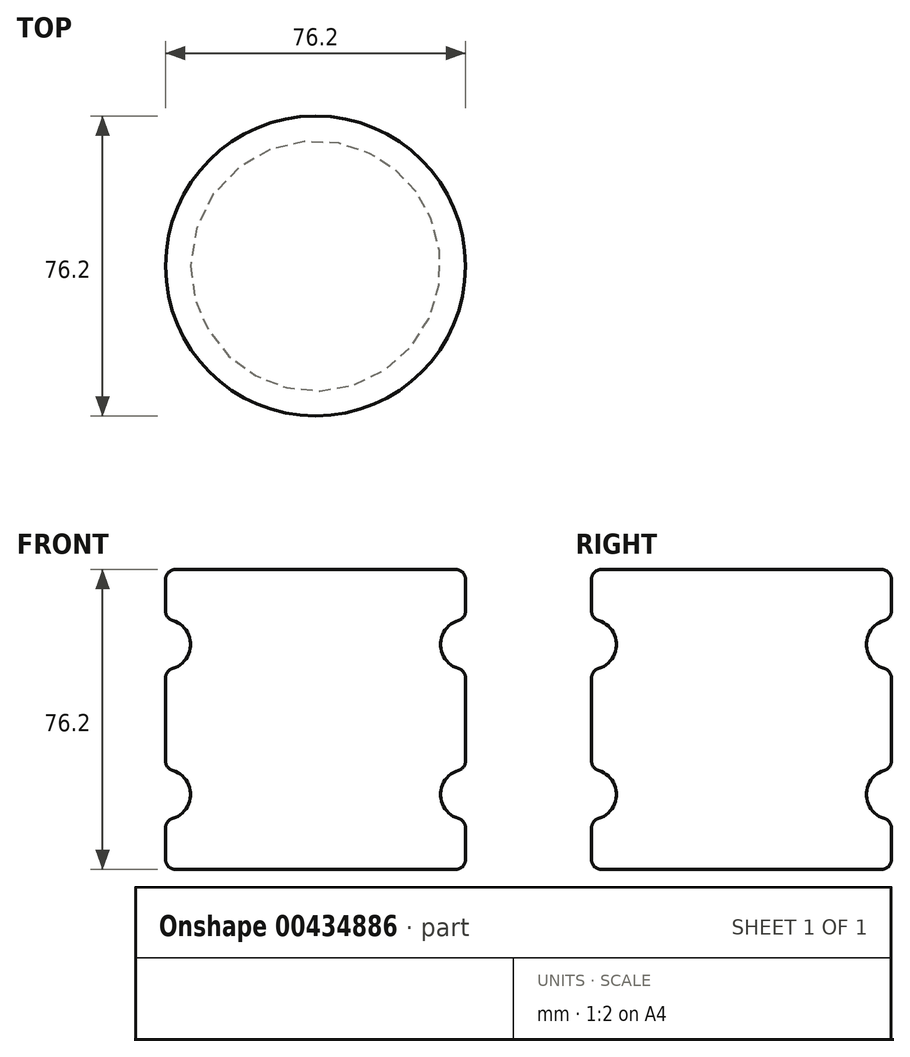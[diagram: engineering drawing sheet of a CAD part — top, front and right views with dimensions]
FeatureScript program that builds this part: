
annotation { "Feature Type Name" : "Feature", "Feature Type Description" : "" }
export const myFeature = defineFeature(function(context is Context, id is Id, definition is map)
    precondition{}
    {
        {
            var Q0;
            Q0=qCreatedBy(makeId("Front.planeOp"),FACE);
            var sketch = newSketch(context, id + "F0", { "sketchPlane" : qUnion([Q0])});
            skLineSegment(sketch, "E0.bottom", {"start": v(0, 0) * mm, "end": v(-38.1, 0) * mm});
            skLineSegment(sketch, "E0.top", {"start": v(0, 76.2) * mm, "end": v(-38.1, 76.2) * mm});
            skLineSegment(sketch, "E0.left", {"start": v(0, 0) * mm, "end": v(0, 76.2) * mm});
            skLineSegment(sketch, "E0.right", {"start": v(-38.1, 0) * mm, "end": v(-38.1, 76.2) * mm});
            skArc(sketch, "E1", {"start": v(0, 25.4) * mm, "mid": v(-6.35, 19.05) * mm, "end": v(0, 12.7) * mm});
            skArc(sketch, "E2", {"start": v(0, 63.5) * mm, "mid": v(-6.35, 57.15) * mm, "end": v(0, 50.8) * mm});
            skSolve(sketch);
        }
        {
            var Q0;
            {var subQ3=sQuery(id+"F0.wireOp",EDGE,"E0.bottom");Q0=makeQuery(id+"F0.imprint","IMPRINT",FACE,{"disambiguationData":[TD([[makeQuery(id+"F0.imprint","IMPRINT",EDGE,{"derivedFrom":subQ3}),-1.0]])]});}
            var Q1;
            Q1=sQuery(id+"F0.wireOp",EDGE,"E0.right");
            revolve(context, id + "F1", {"entities" : qUnion([Q0]), "axis" : qUnion([Q1]), "revolveType" : RevolveType.FULL});
        }
        {
            var Q0;
            Q0=makeQuery(id+"F1.opRevolve","SWEPT_EDGE",EDGE,{"disambiguationData":[OSD([sQuery(id+"F0.wireOp",EDGE,"E0.top"),sQuery(id+"F0.wireOp",EDGE,"E0.left")])]});
            var Q1;
            {var subQ0=sQuery(id+"F0.wireOp",EDGE,"E2");var subQ1=sQuery(id+"F0.wireOp",EDGE,"E0.left");Q1=makeQuery(id+"F1.opRevolve","SWEPT_EDGE",EDGE,{"disambiguationData":[OSD([subQ1,subQ0]),TDD([makeQuery(id+"F0.imprint","INTERSECT",VERTEX,{"disambiguationData":[OD(0.0)],"derivedFrom":[subQ1,subQ0]})])]});}
            var Q2;
            {var subQ0=sQuery(id+"F0.wireOp",EDGE,"E2");var subQ1=sQuery(id+"F0.wireOp",EDGE,"E0.left");Q2=makeQuery(id+"F1.opRevolve","SWEPT_EDGE",EDGE,{"disambiguationData":[OSD([subQ1,subQ0]),TDD([makeQuery(id+"F0.imprint","INTERSECT",VERTEX,{"disambiguationData":[OD(1.0)],"derivedFrom":[subQ1,subQ0]})])]});}
            var Q3;
            {var subQ0=sQuery(id+"F0.wireOp",EDGE,"E1");var subQ1=sQuery(id+"F0.wireOp",EDGE,"E0.left");Q3=makeQuery(id+"F1.opRevolve","SWEPT_EDGE",EDGE,{"disambiguationData":[OSD([subQ1,subQ0]),TDD([makeQuery(id+"F0.imprint","INTERSECT",VERTEX,{"disambiguationData":[OD(0.0)],"derivedFrom":[subQ1,subQ0]})])]});}
            var Q4;
            {var subQ0=sQuery(id+"F0.wireOp",EDGE,"E1");var subQ1=sQuery(id+"F0.wireOp",EDGE,"E0.left");Q4=makeQuery(id+"F1.opRevolve","SWEPT_EDGE",EDGE,{"disambiguationData":[OSD([subQ1,subQ0]),TDD([makeQuery(id+"F0.imprint","INTERSECT",VERTEX,{"disambiguationData":[OD(1.0)],"derivedFrom":[subQ1,subQ0]})])]});}
            var Q5;
            {var subQ0=sQuery(id+"F0.wireOp",EDGE,"E0.left");Q5=makeQuery(id+"F1.opRevolve","SWEPT_FACE",FACE,{"disambiguationData":[OSD([subQ0]),TDD([makeQuery(id+"F0.imprint","IMPRINT",EDGE,{"disambiguationData":[TD([[makeQuery(id+"F0.imprint","INTERSECT",VERTEX,{"derivedFrom":[sQuery(id+"F0.wireOp",EDGE,"E0.bottom"),subQ0]}),-1.0]])],"derivedFrom":subQ0})])]});}
            fillet(context, id + "F2", {"entities" : qUnion([Q0, Q1, Q2, Q3, Q4, Q5]), "radius" : 2.54 * mm, "tangentPropagation" : true, "allowEdgeOverflow" : false});
        }
    });
